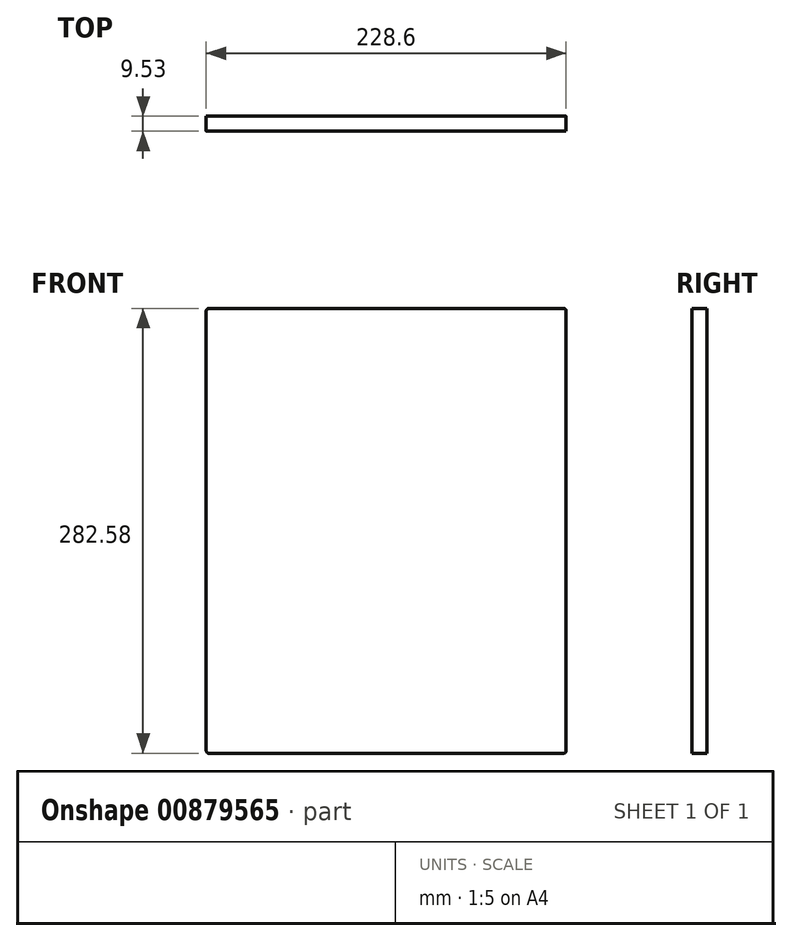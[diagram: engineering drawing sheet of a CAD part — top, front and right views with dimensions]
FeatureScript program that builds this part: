
annotation { "Feature Type Name" : "Feature", "Feature Type Description" : "" }
export const myFeature = defineFeature(function(context is Context, id is Id, definition is map)
    precondition{}
    {
        {
            var Q0;
            Q0=qCreatedBy(makeId("Front.planeOp"),FACE);
            var sketch = newSketch(context, id + "F0", { "sketchPlane" : qUnion([Q0])});
            skLineSegment(sketch, "E0.bottom", {"start": v(114.3, 141.29) * mm, "end": v(-114.3, 141.29) * mm});
            skLineSegment(sketch, "E0.top", {"start": v(114.3, -141.29) * mm, "end": v(-114.3, -141.29) * mm});
            skLineSegment(sketch, "E0.left", {"start": v(114.3, 141.29) * mm, "end": v(114.3, -141.29) * mm});
            skLineSegment(sketch, "E0.right", {"start": v(-114.3, 141.29) * mm, "end": v(-114.3, -141.29) * mm});
            skPoint(sketch, "E0.middle", {"position": v(0, 0) * mm});
            skSolve(sketch);
        }
        {
            var Q0;
            Q0 = qSketchRegion(id + "F0", true);
            extrude(context, id + "F1", {"entities" : qUnion([Q0]), "depth" : 9.52 * mm, "offsetDistance" : 25.4 * mm});
        }
        {
            var Q0;
            Q0=makeQuery(id+"F1.opExtrude","SWEPT_EDGE",EDGE,{"disambiguationData":[OSD([sQuery(id+"F0.wireOp",EDGE,"E0.bottom"),sQuery(id+"F0.wireOp",EDGE,"E0.left")])]});
            var Q1;
            Q1=makeQuery(id+"F1.opExtrude","SWEPT_EDGE",EDGE,{"disambiguationData":[OSD([sQuery(id+"F0.wireOp",EDGE,"E0.bottom"),sQuery(id+"F0.wireOp",EDGE,"E0.right")])]});
            var Q2;
            Q2=makeQuery(id+"F1.opExtrude","SWEPT_EDGE",EDGE,{"disambiguationData":[OSD([sQuery(id+"F0.wireOp",EDGE,"E0.top"),sQuery(id+"F0.wireOp",EDGE,"E0.left")])]});
            var Q3;
            Q3=makeQuery(id+"F1.opExtrude","SWEPT_EDGE",EDGE,{"disambiguationData":[OSD([sQuery(id+"F0.wireOp",EDGE,"E0.top"),sQuery(id+"F0.wireOp",EDGE,"E0.right")])]});
            fillet(context, id + "F2", {"entities" : qUnion([Q0, Q1, Q2, Q3]), "radius" : 1.6 * mm, "tangentPropagation" : true, "allowEdgeOverflow" : false});
        }
    });
